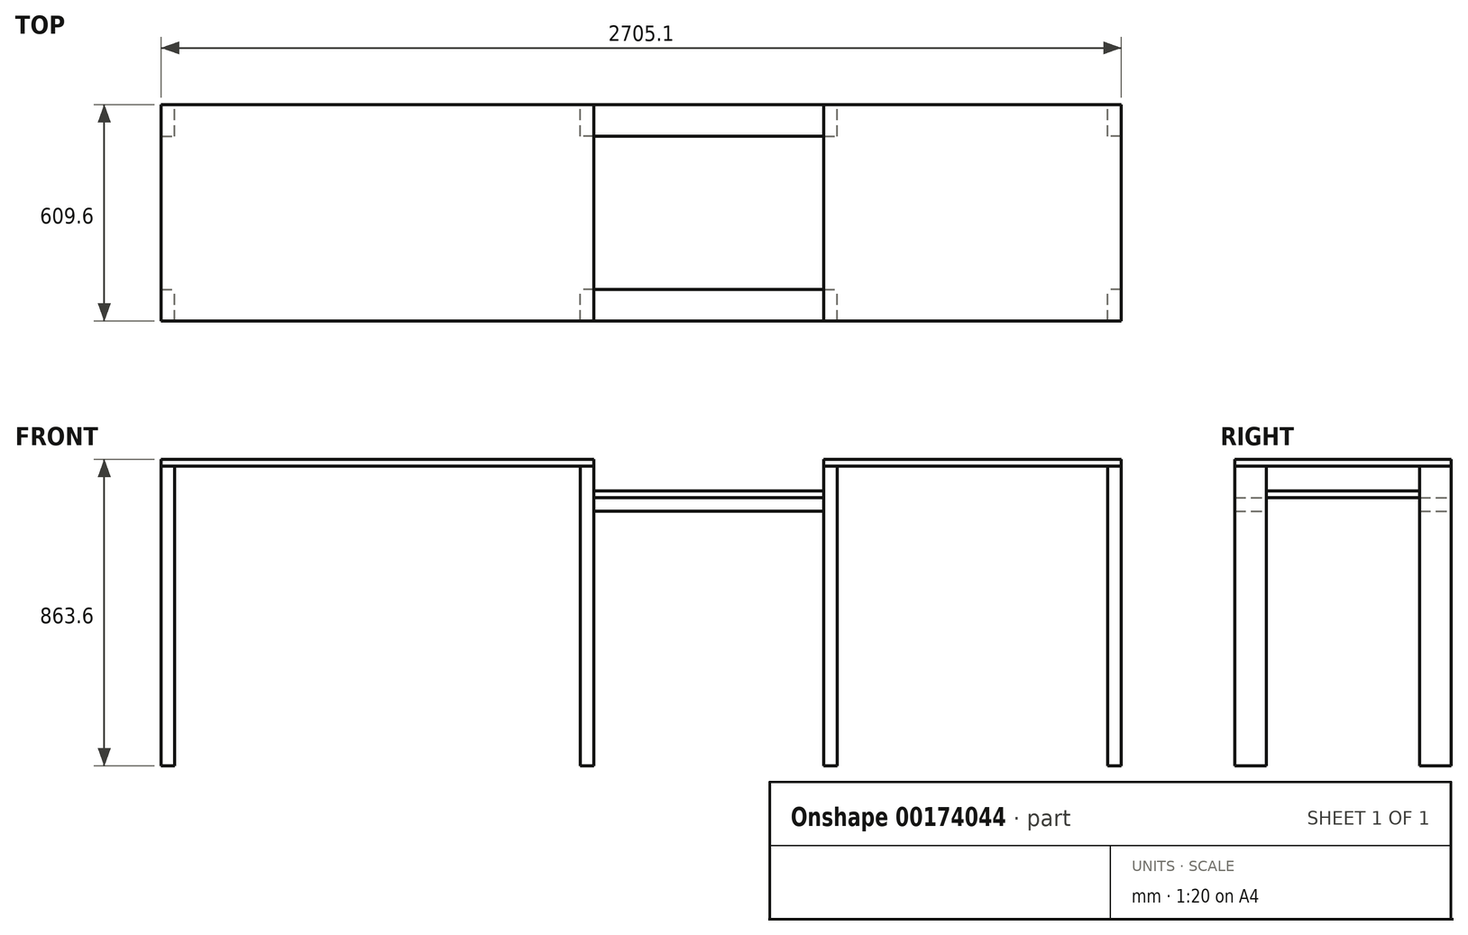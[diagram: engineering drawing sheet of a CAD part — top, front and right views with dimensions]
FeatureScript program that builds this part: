
annotation { "Feature Type Name" : "Feature", "Feature Type Description" : "" }
export const myFeature = defineFeature(function(context is Context, id is Id, definition is map)
    precondition{}
    {
        {
            var Q0;
            Q0=qCreatedBy(makeId("Top.planeOp"),FACE);
            var sketch = newSketch(context, id + "F0", { "sketchPlane" : qUnion([Q0])});
            skLineSegment(sketch, "E0.bottom", {"start": v(-609.6, 0) * mm, "end": v(-571.5, 0) * mm});
            skLineSegment(sketch, "E0.top", {"start": v(-609.6, 88.9) * mm, "end": v(-571.5, 88.9) * mm});
            skLineSegment(sketch, "E0.left", {"start": v(-609.6, 0) * mm, "end": v(-609.6, 88.9) * mm});
            skLineSegment(sketch, "E0.right", {"start": v(-571.5, 0) * mm, "end": v(-571.5, 88.9) * mm});
            skLineSegment(sketch, "E1.bottom", {"start": v(-609.6, 520.7) * mm, "end": v(-571.5, 520.7) * mm});
            skLineSegment(sketch, "E1.top", {"start": v(-609.6, 609.6) * mm, "end": v(-571.5, 609.6) * mm});
            skLineSegment(sketch, "E1.left", {"start": v(-609.6, 520.7) * mm, "end": v(-609.6, 609.6) * mm});
            skLineSegment(sketch, "E1.right", {"start": v(-571.5, 520.7) * mm, "end": v(-571.5, 609.6) * mm});
            skSolve(sketch);
        }
        {
            var Q0;
            Q0=makeQuery(id+"F0.imprint","IMPRINT",FACE,{"disambiguationData":[TD([[makeQuery(id+"F0.imprint","IMPRINT",EDGE,{"derivedFrom":sQuery(id+"F0.wireOp",EDGE,"E1.bottom")}),1.0]])]});
            var Q1;
            Q1=makeQuery(id+"F0.imprint","IMPRINT",FACE,{"disambiguationData":[TD([[makeQuery(id+"F0.imprint","IMPRINT",EDGE,{"derivedFrom":sQuery(id+"F0.wireOp",EDGE,"E0.bottom")}),1.0]])]});
            extrude(context, id + "F1", {"entities" : qUnion([Q0, Q1]), "depth" : 844.55 * mm});
        }
        {
            var Q0;
            Q0=makeQuery(id+"F1.opExtrude","SWEPT_BODY",BODY,{"disambiguationData":[OSD([sQuery(id+"F0.wireOp",EDGE,"E0.bottom"),sQuery(id+"F0.wireOp",EDGE,"E0.top"),sQuery(id+"F0.wireOp",EDGE,"E0.left"),sQuery(id+"F0.wireOp",EDGE,"E0.right")])]});
            var Q1;
            Q1=makeQuery(id+"F1.opExtrude","SWEPT_BODY",BODY,{"disambiguationData":[OSD([sQuery(id+"F0.wireOp",EDGE,"E1.bottom"),sQuery(id+"F0.wireOp",EDGE,"E1.top"),sQuery(id+"F0.wireOp",EDGE,"E1.left"),sQuery(id+"F0.wireOp",EDGE,"E1.right")])]});
            var Q2;
            Q2=qCreatedBy(makeId("Right.planeOp"),FACE);
            mirror(context, id + "F2", {"entities" : qUnion([Q0, Q1]), "mirrorPlane" : qUnion([Q2])});
        }
        {
            var Q0;
            Q0=qCreatedBy(makeId("Top.planeOp"),FACE);
            var Q1;
            Q1=makeQuery(id+"F1.opExtrude","CAP_VERTEX",VERTEX,{"disambiguationData":[OSD([sQuery(id+"F0.wireOp",EDGE,"E0.bottom"),sQuery(id+"F0.wireOp",EDGE,"E0.left")])],"isStart":false});
            cPlane(context, id + "F3", {"entities" : qUnion([Q0, Q1]), "cplaneType" : CPlaneType.PLANE_POINT, "offset" : 25.4 * mm, "width" : 152.4 * mm, "height" : 152.4 * mm});
        }
        {
            var Q0;
            Q0=qCreatedBy(id+"F3.planeOp",FACE);
            var sketch = newSketch(context, id + "F4", { "sketchPlane" : qUnion([Q0])});
            skLineSegment(sketch, "E2.0.0", {"start": v(-609.6, 609.6) * mm, "end": v(-609.6, 520.7) * mm, "construction": true});
            skLineSegment(sketch, "E2.0.1", {"start": v(-609.6, 520.7) * mm, "end": v(-571.5, 520.7) * mm, "construction": true});
            skLineSegment(sketch, "E2.0.2", {"start": v(-571.5, 520.7) * mm, "end": v(-571.5, 609.6) * mm, "construction": true});
            skLineSegment(sketch, "E2.0.3", {"start": v(-571.5, 609.6) * mm, "end": v(-609.6, 609.6) * mm, "construction": true});
            skLineSegment(sketch, "E3.0.0", {"start": v(-609.6, 88.9) * mm, "end": v(-609.6, 0) * mm, "construction": true});
            skLineSegment(sketch, "E3.0.1", {"start": v(-609.6, 0) * mm, "end": v(-571.5, 0) * mm, "construction": true});
            skLineSegment(sketch, "E3.0.2", {"start": v(-571.5, 0) * mm, "end": v(-571.5, 88.9) * mm, "construction": true});
            skLineSegment(sketch, "E3.0.3", {"start": v(-571.5, 88.9) * mm, "end": v(-609.6, 88.9) * mm, "construction": true});
            skLineSegment(sketch, "E4.0.0", {"start": v(609.6, 520.7) * mm, "end": v(609.6, 609.6) * mm, "construction": true});
            skLineSegment(sketch, "E4.0.1", {"start": v(609.6, 609.6) * mm, "end": v(571.5, 609.6) * mm, "construction": true});
            skLineSegment(sketch, "E4.0.2", {"start": v(571.5, 609.6) * mm, "end": v(571.5, 520.7) * mm, "construction": true});
            skLineSegment(sketch, "E4.0.3", {"start": v(571.5, 520.7) * mm, "end": v(609.6, 520.7) * mm, "construction": true});
            skLineSegment(sketch, "E5.0.0", {"start": v(609.6, 0) * mm, "end": v(609.6, 88.9) * mm, "construction": true});
            skLineSegment(sketch, "E5.0.1", {"start": v(609.6, 88.9) * mm, "end": v(571.5, 88.9) * mm, "construction": true});
            skLineSegment(sketch, "E5.0.2", {"start": v(571.5, 88.9) * mm, "end": v(571.5, 0) * mm, "construction": true});
            skLineSegment(sketch, "E5.0.3", {"start": v(571.5, 0) * mm, "end": v(609.6, 0) * mm, "construction": true});
            skLineSegment(sketch, "E6.bottom", {"start": v(-609.6, 609.6) * mm, "end": v(609.6, 609.6) * mm});
            skLineSegment(sketch, "E6.top", {"start": v(-609.6, 0) * mm, "end": v(609.6, 0) * mm});
            skLineSegment(sketch, "E6.left", {"start": v(-609.6, 609.6) * mm, "end": v(-609.6, 0) * mm});
            skLineSegment(sketch, "E6.right", {"start": v(609.6, 609.6) * mm, "end": v(609.6, 0) * mm});
            skSolve(sketch);
        }
        {
            var Q0;
            Q0=makeQuery(id+"F4.imprint","IMPRINT",FACE,{"disambiguationData":[TD([[makeQuery(id+"F4.imprint","IMPRINT",EDGE,{"derivedFrom":sQuery(id+"F4.wireOp",EDGE,"E6.bottom")}),-1.0]])]});
            extrude(context, id + "F5", {"entities" : qUnion([Q0]), "depth" : 19.05 * mm});
        }
        {
            var Q0;
            Q0=makeQuery(id+"F2.opPattern","COPY",FACE,{"derivedFrom":makeQuery(id+"F1.opExtrude","SWEPT_FACE",FACE,{"disambiguationData":[OSD([sQuery(id+"F0.wireOp",EDGE,"E1.left")])]}),"instanceName":"1"});
            var sketch = newSketch(context, id + "F6", { "sketchPlane" : qUnion([Q0])});
            skLineSegment(sketch, "E7.0.0", {"start": v(0, 0) * mm, "end": v(88.9, 0) * mm});
            skLineSegment(sketch, "E7.0.1", {"start": v(88.9, 0) * mm, "end": v(88.9, 844.55) * mm});
            skLineSegment(sketch, "E7.0.2", {"start": v(88.9, 844.55) * mm, "end": v(0, 844.55) * mm});
            skLineSegment(sketch, "E7.0.3", {"start": v(0, 844.55) * mm, "end": v(0, 0) * mm});
            skLineSegment(sketch, "E8.0.0", {"start": v(520.7, 0) * mm, "end": v(609.6, 0) * mm});
            skLineSegment(sketch, "E8.0.1", {"start": v(609.6, 0) * mm, "end": v(609.6, 844.55) * mm});
            skLineSegment(sketch, "E8.0.2", {"start": v(609.6, 844.55) * mm, "end": v(520.7, 844.55) * mm});
            skLineSegment(sketch, "E8.0.3", {"start": v(520.7, 844.55) * mm, "end": v(520.7, 0) * mm});
            skLineSegment(sketch, "E9.bottom", {"start": v(0, 755.65) * mm, "end": v(88.9, 755.65) * mm});
            skLineSegment(sketch, "E9.top", {"start": v(0, 717.55) * mm, "end": v(88.9, 717.55) * mm});
            skLineSegment(sketch, "E9.left", {"start": v(0, 755.65) * mm, "end": v(0, 717.55) * mm});
            skLineSegment(sketch, "E9.right", {"start": v(88.9, 755.65) * mm, "end": v(88.9, 717.55) * mm});
            skLineSegment(sketch, "E10.bottom", {"start": v(520.7, 755.65) * mm, "end": v(609.6, 755.65) * mm});
            skLineSegment(sketch, "E10.top", {"start": v(520.7, 717.55) * mm, "end": v(609.6, 717.55) * mm});
            skLineSegment(sketch, "E10.left", {"start": v(520.7, 755.65) * mm, "end": v(520.7, 717.55) * mm});
            skLineSegment(sketch, "E10.right", {"start": v(609.6, 755.65) * mm, "end": v(609.6, 717.55) * mm});
            skLineSegment(sketch, "E11.bottom", {"start": v(0, 755.65) * mm, "end": v(609.6, 755.65) * mm});
            skLineSegment(sketch, "E11.top", {"start": v(0, 774.7) * mm, "end": v(609.6, 774.7) * mm});
            skLineSegment(sketch, "E11.left", {"start": v(0, 755.65) * mm, "end": v(0, 774.7) * mm});
            skLineSegment(sketch, "E11.right", {"start": v(609.6, 755.65) * mm, "end": v(609.6, 774.7) * mm});
            skSolve(sketch);
        }
        {
            var Q0;
            Q0=makeQuery(id+"F6.imprint","IMPRINT",FACE,{"disambiguationData":[TD([[makeQuery(id+"F6.imprint","IMPRINT",EDGE,{"derivedFrom":sQuery(id+"F6.wireOp",EDGE,"E9.top")}),1.0]])]});
            var Q1;
            Q1=makeQuery(id+"F6.imprint","IMPRINT",FACE,{"disambiguationData":[TD([[makeQuery(id+"F6.imprint","IMPRINT",EDGE,{"derivedFrom":sQuery(id+"F6.wireOp",EDGE,"E10.top")}),1.0]])]});
            extrude(context, id + "F7", {"entities" : qUnion([Q0, Q1]), "depth" : 647.7 * mm});
        }
        {
            var Q0;
            {var subQ5=sQuery(id+"F6.wireOp",EDGE,"E11.left");Q0=makeQuery(id+"F6.imprint","IMPRINT",FACE,{"disambiguationData":[TD([[makeQuery(id+"F6.imprint","IMPRINT",EDGE,{"derivedFrom":subQ5}),-1.0]])]});}
            var Q1;
            {var subQ5=sQuery(id+"F6.wireOp",EDGE,"E11.right");Q1=makeQuery(id+"F6.imprint","IMPRINT",FACE,{"disambiguationData":[TD([[makeQuery(id+"F6.imprint","IMPRINT",EDGE,{"derivedFrom":subQ5}),-1.0]])]});}
            var Q2;
            {var subQ1=sQuery(id+"F6.wireOp",EDGE,"E7.0.1");var subQ3=sQuery(id+"F6.wireOp",EDGE,"E11.top");var subQ4=makeQuery(id+"F6.imprint","INTERSECT",VERTEX,{"derivedFrom":[subQ1,subQ3]});Q2=makeQuery(id+"F6.imprint","IMPRINT",FACE,{"disambiguationData":[TD([[makeQuery(id+"F6.imprint","IMPRINT",EDGE,{"disambiguationData":[TD([[subQ4,-1.0]])],"derivedFrom":subQ3}),-1.0]])]});}
            var Q3;
            Q3=makeQuery(id+"F7.opExtrude","CAP_FACE",FACE,{"disambiguationData":[OSD([sQuery(id+"F6.wireOp",EDGE,"E9.top"),sQuery(id+"F6.wireOp",EDGE,"E9.left"),sQuery(id+"F6.wireOp",EDGE,"E9.right"),sQuery(id+"F6.wireOp",EDGE,"E11.bottom")])],"isStart":false});
            extrude(context, id + "F8", {"entities" : qUnion([Q0, Q1, Q2]), "endBound" : BoundingType.UP_TO_SURFACE, "endBoundEntityFace" : qUnion([Q3]), "depth" : 25.4 * mm});
        }
        {
            var Q0;
            Q0=makeQuery(id+"F8.opExtrude","SWEPT_EDGE",EDGE,{"disambiguationData":[OSD([sQuery(id+"F6.wireOp",EDGE,"E7.0.3"),sQuery(id+"F6.wireOp",EDGE,"E11.top"),sQuery(id+"F6.wireOp",EDGE,"E11.left")])]});
            cPoint(context, id + "F9", {"entities" : qUnion([Q0]), "parameter" : 0.5});
        }
        {
            var Q0;
            Q0=qCreatedBy(makeId("Right.planeOp"),FACE);
            var Q1;
            Q1 = qCreatedBy(id + "F9" ,VERTEX);
            cPlane(context, id + "F10", {"entities" : qUnion([Q0, Q1]), "cplaneType" : CPlaneType.PLANE_POINT, "offset" : 25.4 * mm, "width" : 152.4 * mm, "height" : 152.4 * mm});
        }
        {
            var Q0;
            Q0=makeQuery(id+"F2.opPattern","COPY",BODY,{"derivedFrom":makeQuery(id+"F1.opExtrude","SWEPT_BODY",BODY,{"disambiguationData":[OSD([sQuery(id+"F0.wireOp",EDGE,"E0.bottom"),sQuery(id+"F0.wireOp",EDGE,"E0.top"),sQuery(id+"F0.wireOp",EDGE,"E0.left"),sQuery(id+"F0.wireOp",EDGE,"E0.right")])]}),"instanceName":"1"});
            var Q1;
            Q1=makeQuery(id+"F2.opPattern","COPY",BODY,{"derivedFrom":makeQuery(id+"F1.opExtrude","SWEPT_BODY",BODY,{"disambiguationData":[OSD([sQuery(id+"F0.wireOp",EDGE,"E1.bottom"),sQuery(id+"F0.wireOp",EDGE,"E1.top"),sQuery(id+"F0.wireOp",EDGE,"E1.left"),sQuery(id+"F0.wireOp",EDGE,"E1.right")])]}),"instanceName":"1"});
            var Q2;
            Q2=qCreatedBy(id+"F10.planeOp",FACE);
            mirror(context, id + "F11", {"entities" : qUnion([Q0, Q1]), "mirrorPlane" : qUnion([Q2])});
        }
        {
            var Q0;
            Q0=makeQuery(id+"F11.opPattern","COPY",FACE,{"derivedFrom":makeQuery(id+"F2.opPattern","COPY",FACE,{"derivedFrom":makeQuery(id+"F1.opExtrude","SWEPT_FACE",FACE,{"disambiguationData":[OSD([sQuery(id+"F0.wireOp",EDGE,"E0.right")])]}),"instanceName":"1"}),"instanceName":"1"});
            cPlane(context, id + "F12", {"entities" : qUnion([Q0]), "cplaneType" : CPlaneType.OFFSET, "offset" : 381 * mm, "width" : 152.4 * mm, "height" : 152.4 * mm});
        }
        {
            var Q0;
            Q0=makeQuery(id+"F11.opPattern","COPY",BODY,{"derivedFrom":makeQuery(id+"F2.opPattern","COPY",BODY,{"derivedFrom":makeQuery(id+"F1.opExtrude","SWEPT_BODY",BODY,{"disambiguationData":[OSD([sQuery(id+"F0.wireOp",EDGE,"E0.bottom"),sQuery(id+"F0.wireOp",EDGE,"E0.top"),sQuery(id+"F0.wireOp",EDGE,"E0.left"),sQuery(id+"F0.wireOp",EDGE,"E0.right")])]}),"instanceName":"1"}),"instanceName":"1"});
            var Q1;
            Q1=makeQuery(id+"F11.opPattern","COPY",BODY,{"derivedFrom":makeQuery(id+"F2.opPattern","COPY",BODY,{"derivedFrom":makeQuery(id+"F1.opExtrude","SWEPT_BODY",BODY,{"disambiguationData":[OSD([sQuery(id+"F0.wireOp",EDGE,"E1.bottom"),sQuery(id+"F0.wireOp",EDGE,"E1.top"),sQuery(id+"F0.wireOp",EDGE,"E1.left"),sQuery(id+"F0.wireOp",EDGE,"E1.right")])]}),"instanceName":"1"}),"instanceName":"1"});
            var Q2;
            Q2=qCreatedBy(id+"F12.planeOp",FACE);
            mirror(context, id + "F13", {"entities" : qUnion([Q0, Q1]), "mirrorPlane" : qUnion([Q2])});
        }
        {
            var Q0;
            Q0=makeQuery(id+"F11.opPattern","COPY",FACE,{"derivedFrom":makeQuery(id+"F2.opPattern","COPY",FACE,{"derivedFrom":makeQuery(id+"F1.opExtrude","SWEPT_FACE",FACE,{"disambiguationData":[OSD([sQuery(id+"F0.wireOp",EDGE,"E0.left")])]}),"instanceName":"1"}),"instanceName":"1"});
            var sketch = newSketch(context, id + "F14", { "sketchPlane" : qUnion([Q0])});
            skLineSegment(sketch, "E12.0.0", {"start": v(-609.6, 0) * mm, "end": v(-520.7, 0) * mm});
            skLineSegment(sketch, "E12.0.1", {"start": v(-520.7, 0) * mm, "end": v(-520.7, 844.55) * mm});
            skLineSegment(sketch, "E12.0.2", {"start": v(-520.7, 844.55) * mm, "end": v(-609.6, 844.55) * mm});
            skLineSegment(sketch, "E12.0.3", {"start": v(-609.6, 844.55) * mm, "end": v(-609.6, 0) * mm});
            skLineSegment(sketch, "E13.0.0", {"start": v(-88.9, 0) * mm, "end": v(0, 0) * mm});
            skLineSegment(sketch, "E13.0.1", {"start": v(0, 0) * mm, "end": v(0, 844.55) * mm});
            skLineSegment(sketch, "E13.0.2", {"start": v(0, 844.55) * mm, "end": v(-88.9, 844.55) * mm});
            skLineSegment(sketch, "E13.0.3", {"start": v(-88.9, 844.55) * mm, "end": v(-88.9, 0) * mm});
            skLineSegment(sketch, "E14.bottom", {"start": v(-609.6, 844.55) * mm, "end": v(0, 844.55) * mm});
            skLineSegment(sketch, "E14.top", {"start": v(-609.6, 863.6) * mm, "end": v(0, 863.6) * mm});
            skLineSegment(sketch, "E14.left", {"start": v(-609.6, 844.55) * mm, "end": v(-609.6, 863.6) * mm});
            skLineSegment(sketch, "E14.right", {"start": v(0, 844.55) * mm, "end": v(0, 863.6) * mm});
            skSolve(sketch);
        }
        {
            var Q0;
            Q0=makeQuery(id+"F14.imprint","IMPRINT",FACE,{"disambiguationData":[TD([[makeQuery(id+"F14.imprint","IMPRINT",EDGE,{"derivedFrom":sQuery(id+"F14.wireOp",EDGE,"E14.top")}),-1.0]])]});
            var Q1;
            Q1=makeQuery(id+"F13.opPattern","COPY",FACE,{"derivedFrom":makeQuery(id+"F11.opPattern","COPY",FACE,{"derivedFrom":makeQuery(id+"F2.opPattern","COPY",FACE,{"derivedFrom":makeQuery(id+"F1.opExtrude","SWEPT_FACE",FACE,{"disambiguationData":[OSD([sQuery(id+"F0.wireOp",EDGE,"E0.left")])]}),"instanceName":"1"}),"instanceName":"1"}),"instanceName":"1"});
            extrude(context, id + "F15", {"entities" : qUnion([Q0]), "endBound" : BoundingType.UP_TO_SURFACE, "oppositeDirection" : true, "endBoundEntityFace" : qUnion([Q1]), "depth" : 25.4 * mm});
        }
    });
